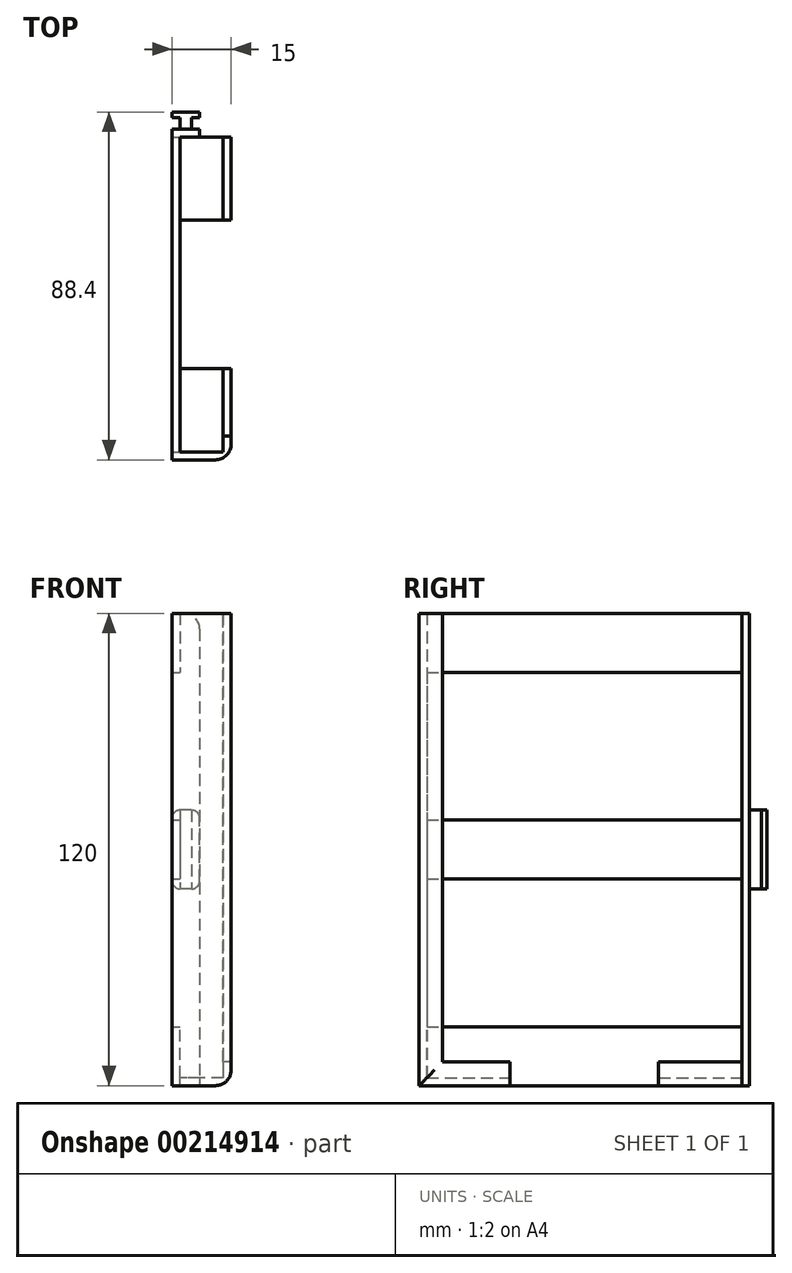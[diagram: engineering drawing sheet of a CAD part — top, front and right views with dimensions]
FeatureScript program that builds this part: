
annotation { "Feature Type Name" : "Feature", "Feature Type Description" : "" }
export const myFeature = defineFeature(function(context is Context, id is Id, definition is map)
    precondition{}
    {
        {
            var Q0;
            Q0=qCreatedBy(makeId("Front.planeOp"),FACE);
            var sketch = newSketch(context, id + "F0", { "sketchPlane" : qUnion([Q0])});
            skLineSegment(sketch, "E0.bottom", {"start": v(3.5, -10) * mm, "end": v(-3.5, -10) * mm});
            skLineSegment(sketch, "E0.top", {"start": v(3.5, 10) * mm, "end": v(-3.5, 10) * mm});
            skLineSegment(sketch, "E0.left", {"start": v(3.5, -10) * mm, "end": v(3.5, 10) * mm});
            skLineSegment(sketch, "E0.right", {"start": v(-3.5, -10) * mm, "end": v(-3.5, 10) * mm});
            skPoint(sketch, "E0.middle", {"position": v(0, 0) * mm});
            skSolve(sketch);
        }
        {
            var Q0;
            Q0=makeQuery(id+"F0.imprint","IMPRINT",FACE,{"disambiguationData":[TD([[makeQuery(id+"F0.imprint","IMPRINT",EDGE,{"derivedFrom":sQuery(id+"F0.wireOp",EDGE,"E0.bottom")}),-1.0]])]});
            extrude(context, id + "F1", {"entities" : qUnion([Q0]), "depth" : 1.4 * mm});
        }
        {
            var Q0;
            Q0=makeQuery(id+"F1.opExtrude","CAP_FACE",FACE,{"disambiguationData":[OSD([sQuery(id+"F0.wireOp",EDGE,"E0.bottom"),sQuery(id+"F0.wireOp",EDGE,"E0.top"),sQuery(id+"F0.wireOp",EDGE,"E0.left"),sQuery(id+"F0.wireOp",EDGE,"E0.right")])],"isStart":false});
            var sketch = newSketch(context, id + "F2", { "sketchPlane" : qUnion([Q0])});
            skLineSegment(sketch, "E1.bottom", {"start": v(1.5, 10) * mm, "end": v(-1.5, 10) * mm});
            skLineSegment(sketch, "E1.top", {"start": v(1.5, -10) * mm, "end": v(-1.5, -10) * mm});
            skLineSegment(sketch, "E1.left", {"start": v(1.5, 10) * mm, "end": v(1.5, -10) * mm});
            skLineSegment(sketch, "E1.right", {"start": v(-1.5, 10) * mm, "end": v(-1.5, -10) * mm});
            skPoint(sketch, "E1.middle", {"position": v(0, 0) * mm});
            skSolve(sketch);
        }
        {
            var Q0;
            Q0=makeQuery(id+"F2.imprint","IMPRINT",FACE,{"disambiguationData":[TD([[makeQuery(id+"F2.imprint","IMPRINT",EDGE,{"derivedFrom":sQuery(id+"F2.wireOp",EDGE,"E1.bottom")}),1.0]])]});
            extrude(context, id + "F3", {"entities" : qUnion([Q0]), "operationType" : NewBodyOperationType.ADD, "depth" : 3 * mm});
        }
        {
            var Q0;
            Q0=makeQuery(id+"F1.opExtrude","SWEPT_EDGE",EDGE,{"disambiguationData":[OSD([sQuery(id+"F0.wireOp",EDGE,"E0.top"),sQuery(id+"F0.wireOp",EDGE,"E0.left")])]});
            var Q1;
            Q1=makeQuery(id+"F1.opExtrude","SWEPT_EDGE",EDGE,{"disambiguationData":[OSD([sQuery(id+"F0.wireOp",EDGE,"E0.top"),sQuery(id+"F0.wireOp",EDGE,"E0.right")])]});
            var Q2;
            Q2=makeQuery(id+"F1.opExtrude","SWEPT_EDGE",EDGE,{"disambiguationData":[OSD([sQuery(id+"F0.wireOp",EDGE,"E0.bottom"),sQuery(id+"F0.wireOp",EDGE,"E0.left")])]});
            var Q3;
            Q3=makeQuery(id+"F1.opExtrude","SWEPT_EDGE",EDGE,{"disambiguationData":[OSD([sQuery(id+"F0.wireOp",EDGE,"E0.bottom"),sQuery(id+"F0.wireOp",EDGE,"E0.right")])]});
            fillet(context, id + "F4", {"entities" : qUnion([Q0, Q1, Q2, Q3]), "radius" : 2 * mm, "tangentPropagation" : true, "allowEdgeOverflow" : false});
        }
        {
            var Q0;
            Q0=makeQuery(id+"F3.opExtrude","CAP_FACE",FACE,{"disambiguationData":[OSD([sQuery(id+"F2.wireOp",EDGE,"E1.bottom"),sQuery(id+"F2.wireOp",EDGE,"E1.top"),sQuery(id+"F2.wireOp",EDGE,"E1.left"),sQuery(id+"F2.wireOp",EDGE,"E1.right")])],"isStart":false});
            var sketch = newSketch(context, id + "F5", { "sketchPlane" : qUnion([Q0])});
            skLineSegment(sketch, "E2.bottom", {"start": v(3.5, 60) * mm, "end": v(-3.5, 60) * mm});
            skLineSegment(sketch, "E2.top", {"start": v(3.5, -60) * mm, "end": v(-3.5, -60) * mm});
            skLineSegment(sketch, "E2.left", {"start": v(3.5, 60) * mm, "end": v(3.5, -60) * mm});
            skLineSegment(sketch, "E2.right", {"start": v(-3.5, 60) * mm, "end": v(-3.5, -60) * mm});
            skPoint(sketch, "E2.middle", {"position": v(0, 0) * mm});
            skSolve(sketch);
        }
        {
            var Q0;
            Q0 = qSketchRegion(id + "F5", true);
            extrude(context, id + "F6", {"entities" : qUnion([Q0]), "operationType" : NewBodyOperationType.ADD, "depth" : 2 * mm});
        }
        {
            var Q0;
            Q0=makeQuery(id+"F6.opExtrude","CAP_FACE",FACE,{"disambiguationData":[OSD([sQuery(id+"F5.wireOp",EDGE,"E2.bottom"),sQuery(id+"F5.wireOp",EDGE,"E2.top"),sQuery(id+"F5.wireOp",EDGE,"E2.left"),sQuery(id+"F5.wireOp",EDGE,"E2.right")])],"isStart":false});
            var sketch = newSketch(context, id + "F7", { "sketchPlane" : qUnion([Q0])});
            skLineSegment(sketch, "E3.bottom", {"start": v(-3.5, 60) * mm, "end": v(-1.5, 60) * mm});
            skLineSegment(sketch, "E3.top", {"start": v(-3.5, 45) * mm, "end": v(-1.5, 45) * mm});
            skLineSegment(sketch, "E3.left", {"start": v(-3.5, 60) * mm, "end": v(-3.5, 45) * mm});
            skLineSegment(sketch, "E3.right", {"start": v(-1.5, 60) * mm, "end": v(-1.5, 45) * mm});
            skLineSegment(sketch, "E4.bottom", {"start": v(-3.5, -60) * mm, "end": v(-1.5, -60) * mm});
            skLineSegment(sketch, "E4.top", {"start": v(-3.5, -45) * mm, "end": v(-1.5, -45) * mm});
            skLineSegment(sketch, "E4.left", {"start": v(-3.5, -60) * mm, "end": v(-3.5, -45) * mm});
            skLineSegment(sketch, "E4.right", {"start": v(-1.5, -60) * mm, "end": v(-1.5, -45) * mm});
            skLineSegment(sketch, "E5.bottom", {"start": v(-3.5, 7.5) * mm, "end": v(-1.5, 7.5) * mm});
            skLineSegment(sketch, "E5.top", {"start": v(-3.5, -7.5) * mm, "end": v(-1.5, -7.5) * mm});
            skLineSegment(sketch, "E5.left", {"start": v(-3.5, 7.5) * mm, "end": v(-3.5, -7.5) * mm});
            skLineSegment(sketch, "E5.right", {"start": v(-1.5, 7.5) * mm, "end": v(-1.5, -7.5) * mm});
            skPoint(sketch, "E6", {"position": v(-3.5, 0) * mm});
            skSolve(sketch);
        }
        {
            var Q0;
            Q0 = qSketchRegion(id + "F7", true);
            extrude(context, id + "F8", {"entities" : qUnion([Q0]), "operationType" : NewBodyOperationType.ADD, "depth" : 80 * mm});
        }
        {
            var Q0;
            Q0=makeQuery(id+"F8.opExtrude","CAP_FACE",FACE,{"disambiguationData":[OSD([sQuery(id+"F7.wireOp",EDGE,"E3.bottom"),sQuery(id+"F7.wireOp",EDGE,"E3.top"),sQuery(id+"F7.wireOp",EDGE,"E3.left"),sQuery(id+"F7.wireOp",EDGE,"E3.right")])],"isStart":false});
            var sketch = newSketch(context, id + "F9", { "sketchPlane" : qUnion([Q0])});
            skLineSegment(sketch, "E7.bottom", {"start": v(-3.5, 60) * mm, "end": v(11.5, 60) * mm});
            skLineSegment(sketch, "E7.top", {"start": v(-3.5, -60) * mm, "end": v(11.5, -60) * mm});
            skLineSegment(sketch, "E7.left", {"start": v(-3.5, 60) * mm, "end": v(-3.5, -60) * mm});
            skLineSegment(sketch, "E7.right", {"start": v(11.5, 60) * mm, "end": v(11.5, -60) * mm});
            skSolve(sketch);
        }
        {
            var Q0;
            {var subQ2=sQuery(id+"F9.wireOp",EDGE,"E7.top");Q0=makeQuery(id+"F9.imprint","IMPRINT",FACE,{"disambiguationData":[TD([[makeQuery(id+"F9.imprint","IMPRINT",EDGE,{"derivedFrom":subQ2}),1.0]])]});}
            var Q1;
            {var subQ4=makeQuery(id+"F8.opExtrude","CAP_EDGE",EDGE,{"disambiguationData":[OSD([sQuery(id+"F7.wireOp",EDGE,"E3.top")])],"isStart":false});Q1=makeQuery(id+"F9.imprint","IMPRINT",FACE,{"disambiguationData":[TD([[makeQuery(id+"F9.imprint","IMPRINT",EDGE,{"derivedFrom":subQ4}),1.0]])]});}
            extrude(context, id + "F10", {"entities" : qUnion([Q0, Q1]), "operationType" : NewBodyOperationType.ADD, "depth" : 2 * mm});
        }
        {
            var Q0;
            Q0=makeQuery(id+"F8.opExtrude","SWEPT_FACE",FACE,{"disambiguationData":[OSD([sQuery(id+"F7.wireOp",EDGE,"E4.right")])]});
            var sketch = newSketch(context, id + "F11", { "sketchPlane" : qUnion([Q0])});
            skLineSegment(sketch, "E8.bottom", {"start": v(-86.4, -60) * mm, "end": v(-6.4, -60) * mm});
            skLineSegment(sketch, "E8.top", {"start": v(-86.4, -58) * mm, "end": v(-6.4, -58) * mm});
            skLineSegment(sketch, "E8.left", {"start": v(-86.4, -60) * mm, "end": v(-86.4, -58) * mm});
            skLineSegment(sketch, "E8.right", {"start": v(-6.4, -60) * mm, "end": v(-6.4, -58) * mm});
            skSolve(sketch);
        }
        {
            var Q0;
            Q0=makeQuery(id+"F11.imprint","IMPRINT",FACE,{"disambiguationData":[TD([[makeQuery(id+"F11.imprint","IMPRINT",EDGE,{"derivedFrom":sQuery(id+"F11.wireOp",EDGE,"E8.bottom")}),1.0]])]});
            var Q1;
            Q1=makeQuery(id+"F10.opExtrude","CAP_VERTEX",VERTEX,{"disambiguationData":[OSD([sQuery(id+"F9.wireOp",EDGE,"E7.top"),sQuery(id+"F9.wireOp",EDGE,"E7.right")])],"isStart":true});
            extrude(context, id + "F12", {"entities" : qUnion([Q0]), "operationType" : NewBodyOperationType.ADD, "endBound" : BoundingType.UP_TO_VERTEX, "endBoundEntityVertex" : qUnion([Q1]), "depth" : 25 * mm});
        }
        {
            var Q0;
            Q0=makeQuery(id+"F12.opExtrude","SWEPT_FACE",FACE,{"disambiguationData":[OSD([sQuery(id+"F11.wireOp",EDGE,"E8.top")])]});
            var sketch = newSketch(context, id + "F13", { "sketchPlane" : qUnion([Q0])});
            skLineSegment(sketch, "E9.bottom", {"start": v(11.5, -27.55) * mm, "end": v(-1.5, -27.55) * mm});
            skLineSegment(sketch, "E9.top", {"start": v(11.5, -65.25) * mm, "end": v(-1.5, -65.25) * mm});
            skLineSegment(sketch, "E9.left", {"start": v(11.5, -27.55) * mm, "end": v(11.5, -65.25) * mm});
            skLineSegment(sketch, "E9.right", {"start": v(-1.5, -27.55) * mm, "end": v(-1.5, -65.25) * mm});
            skPoint(sketch, "E9.middle", {"position": v(5, -46.4) * mm});
            skPoint(sketch, "E9.middle.positionSnap0", {"position": v(5, -86.4) * mm});
            skPoint(sketch, "E9.middle.positionSnap1", {"position": v(-1.5, -46.4) * mm});
            skPoint(sketch, "E9.centerSnap0", {"position": v(5, -86.4) * mm});
            skPoint(sketch, "E9.centerSnap1", {"position": v(-1.5, -46.4) * mm});
            skSolve(sketch);
        }
        {
            var Q0;
            Q0=makeQuery(id+"F13.imprint","IMPRINT",FACE,{"disambiguationData":[TD([[makeQuery(id+"F13.imprint","IMPRINT",EDGE,{"derivedFrom":sQuery(id+"F13.wireOp",EDGE,"E9.bottom")}),1.0]])]});
            extrude(context, id + "F14", {"entities" : qUnion([Q0]), "operationType" : NewBodyOperationType.REMOVE, "endBound" : BoundingType.THROUGH_ALL, "oppositeDirection" : true, "depth" : 25 * mm});
        }
        {
            var Q0;
            {var subQ1=sQuery(id+"F11.wireOp",EDGE,"E8.top");Q0=makeQuery(id+"F14.boolean.opBoolean","SPLIT",FACE,{"disambiguationData":[TD([makeQuery(id+"F14.opExtrude","SWEPT_FACE",FACE,{"disambiguationData":[OSD([sQuery(id+"F13.wireOp",EDGE,"E9.top")])]})])],"derivedFrom":makeQuery(id+"F12.opExtrude","SWEPT_FACE",FACE,{"disambiguationData":[OSD([subQ1])]})});}
            var sketch = newSketch(context, id + "F15", { "sketchPlane" : qUnion([Q0])});
            skLineSegment(sketch, "E10.bottom", {"start": v(11.5, -86.4) * mm, "end": v(9.5, -86.4) * mm});
            skLineSegment(sketch, "E10.top", {"start": v(11.5, -65.25) * mm, "end": v(9.5, -65.25) * mm});
            skLineSegment(sketch, "E10.left", {"start": v(11.5, -86.4) * mm, "end": v(11.5, -65.25) * mm});
            skLineSegment(sketch, "E10.right", {"start": v(9.5, -86.4) * mm, "end": v(9.5, -65.25) * mm});
            skSolve(sketch);
        }
        {
            var Q0;
            {var subQ0=sQuery(id+"F5.wireOp",EDGE,"E2.left");var subQ2=sQuery(id+"F11.wireOp",EDGE,"E8.top");Q0=makeQuery(id+"F14.boolean.opBoolean","SPLIT",FACE,{"disambiguationData":[TD([makeQuery(id+"F6.opExtrude","SWEPT_FACE",FACE,{"disambiguationData":[OSD([subQ0])]})])],"derivedFrom":makeQuery(id+"F12.opExtrude","SWEPT_FACE",FACE,{"disambiguationData":[OSD([subQ2])]})});}
            var sketch = newSketch(context, id + "F16", { "sketchPlane" : qUnion([Q0])});
            skLineSegment(sketch, "E11.bottom", {"start": v(11.5, -27.55) * mm, "end": v(9.5, -27.55) * mm});
            skLineSegment(sketch, "E11.top", {"start": v(11.5, -6.4) * mm, "end": v(9.5, -6.4) * mm});
            skLineSegment(sketch, "E11.left", {"start": v(11.5, -27.55) * mm, "end": v(11.5, -6.4) * mm});
            skLineSegment(sketch, "E11.right", {"start": v(9.5, -27.55) * mm, "end": v(9.5, -6.4) * mm});
            skSolve(sketch);
        }
        {
            var Q0;
            Q0=makeQuery(id+"F15.imprint","IMPRINT",FACE,{"disambiguationData":[TD([[makeQuery(id+"F15.imprint","IMPRINT",EDGE,{"derivedFrom":sQuery(id+"F15.wireOp",EDGE,"E10.bottom")}),-1.0]])]});
            var Q1;
            Q1=makeQuery(id+"F16.imprint","IMPRINT",FACE,{"disambiguationData":[TD([[makeQuery(id+"F16.imprint","IMPRINT",EDGE,{"derivedFrom":sQuery(id+"F16.wireOp",EDGE,"E11.bottom")}),-1.0]])]});
            extrude(context, id + "F17", {"entities" : qUnion([Q0, Q1]), "operationType" : NewBodyOperationType.ADD, "depth" : 4 * mm});
        }
        {
            var Q0;
            Q0=makeQuery(id+"F10.opExtrude","CAP_FACE",FACE,{"disambiguationData":[OSD([sQuery(id+"F9.wireOp",EDGE,"E7.bottom"),sQuery(id+"F9.wireOp",EDGE,"E7.top"),sQuery(id+"F9.wireOp",EDGE,"E7.left"),sQuery(id+"F9.wireOp",EDGE,"E7.right")])],"isStart":true});
            var sketch = newSketch(context, id + "F18", { "sketchPlane" : qUnion([Q0])});
            skLineSegment(sketch, "E12.bottom", {"start": v(-11.5, -54) * mm, "end": v(-9.5, -54) * mm});
            skLineSegment(sketch, "E12.top", {"start": v(-11.5, 60) * mm, "end": v(-9.5, 60) * mm});
            skLineSegment(sketch, "E12.left", {"start": v(-11.5, -54) * mm, "end": v(-11.5, 60) * mm});
            skLineSegment(sketch, "E12.right", {"start": v(-9.5, -54) * mm, "end": v(-9.5, 60) * mm});
            skSolve(sketch);
        }
        {
            var Q0;
            Q0=makeQuery(id+"F18.imprint","IMPRINT",FACE,{"disambiguationData":[TD([[makeQuery(id+"F18.imprint","IMPRINT",EDGE,{"derivedFrom":sQuery(id+"F18.wireOp",EDGE,"E12.bottom")}),1.0]])]});
            extrude(context, id + "F19", {"entities" : qUnion([Q0]), "operationType" : NewBodyOperationType.ADD, "depth" : 4 * mm});
        }
        {
            var Q0;
            {var subQ0=sQuery(id+"F9.wireOp",EDGE,"E7.top");var subQ1=sQuery(id+"F11.wireOp",EDGE,"E8.right");var subQ2=sQuery(id+"F9.wireOp",EDGE,"E7.right");var subQ3=sQuery(id+"F11.wireOp",EDGE,"E8.bottom");Q0=makeQuery(id+"F14.boolean.opBoolean","SPLIT",EDGE,{"disambiguationData":[TD([makeQuery(id+"F12.opExtrude","SWEPT_FACE",FACE,{"disambiguationData":[OSD([subQ1])]})])],"derivedFrom":makeQuery(id+"F12.boolean.opBoolean","MERGE",EDGE,{"derivedFrom":[makeQuery(id+"F10.opExtrude","SWEPT_EDGE",EDGE,{"disambiguationData":[OSD([subQ0,subQ2])]}),makeQuery(id+"F12.opExtrude","CAP_EDGE",EDGE,{"disambiguationData":[OSD([subQ3])],"isStart":false})]})});}
            var Q1;
            {var subQ0=sQuery(id+"F9.wireOp",EDGE,"E7.top");var subQ1=sQuery(id+"F9.wireOp",EDGE,"E7.right");var subQ2=sQuery(id+"F11.wireOp",EDGE,"E8.bottom");Q1=makeQuery(id+"F14.boolean.opBoolean","SPLIT",EDGE,{"disambiguationData":[TD([makeQuery(id+"F14.opExtrude","SWEPT_FACE",FACE,{"disambiguationData":[OSD([sQuery(id+"F13.wireOp",EDGE,"E9.top")])]})])],"derivedFrom":makeQuery(id+"F12.boolean.opBoolean","MERGE",EDGE,{"derivedFrom":[makeQuery(id+"F10.opExtrude","SWEPT_EDGE",EDGE,{"disambiguationData":[OSD([subQ0,subQ1])]}),makeQuery(id+"F12.opExtrude","CAP_EDGE",EDGE,{"disambiguationData":[OSD([subQ2])],"isStart":false})]})});}
            var Q2;
            Q2=makeQuery(id+"F10.opExtrude","CAP_EDGE",EDGE,{"disambiguationData":[OSD([sQuery(id+"F9.wireOp",EDGE,"E7.right")])],"isStart":false});
            var Q3;
            Q3=makeQuery(id+"F17.opExtrude","CAP_EDGE",EDGE,{"disambiguationData":[OSD([sQuery(id+"F15.wireOp",EDGE,"E10.right")])],"isStart":true});
            var Q4;
            Q4=makeQuery(id+"F19.boolean.opBoolean","MERGE",EDGE,{"derivedFrom":[makeQuery(id+"F17.opExtrude","SWEPT_EDGE",EDGE,{"disambiguationData":[OSD([sQuery(id+"F7.wireOp",EDGE,"E4.right"),sQuery(id+"F11.wireOp",EDGE,"E8.top"),sQuery(id+"F11.wireOp",EDGE,"E8.left"),sQuery(id+"F15.wireOp",EDGE,"E10.bottom"),sQuery(id+"F15.wireOp",EDGE,"E10.right")])]}),makeQuery(id+"F19.opExtrude","CAP_EDGE",EDGE,{"disambiguationData":[OSD([sQuery(id+"F18.wireOp",EDGE,"E12.right")])],"isStart":true})]});
            var Q5;
            Q5=makeQuery(id+"F17.opExtrude","CAP_EDGE",EDGE,{"disambiguationData":[OSD([sQuery(id+"F16.wireOp",EDGE,"E11.right")])],"isStart":true});
            var Q6;
            Q6=makeQuery(id+"F6.opExtrude","SWEPT_EDGE",EDGE,{"disambiguationData":[OSD([sQuery(id+"F5.wireOp",EDGE,"E2.bottom"),sQuery(id+"F5.wireOp",EDGE,"E2.left")])]});
            fillet(context, id + "F20", {"entities" : qUnion([Q0, Q1, Q2, Q3, Q4, Q5, Q6]), "radius" : 4 * mm, "tangentPropagation" : true, "allowEdgeOverflow" : false});
        }
    });
